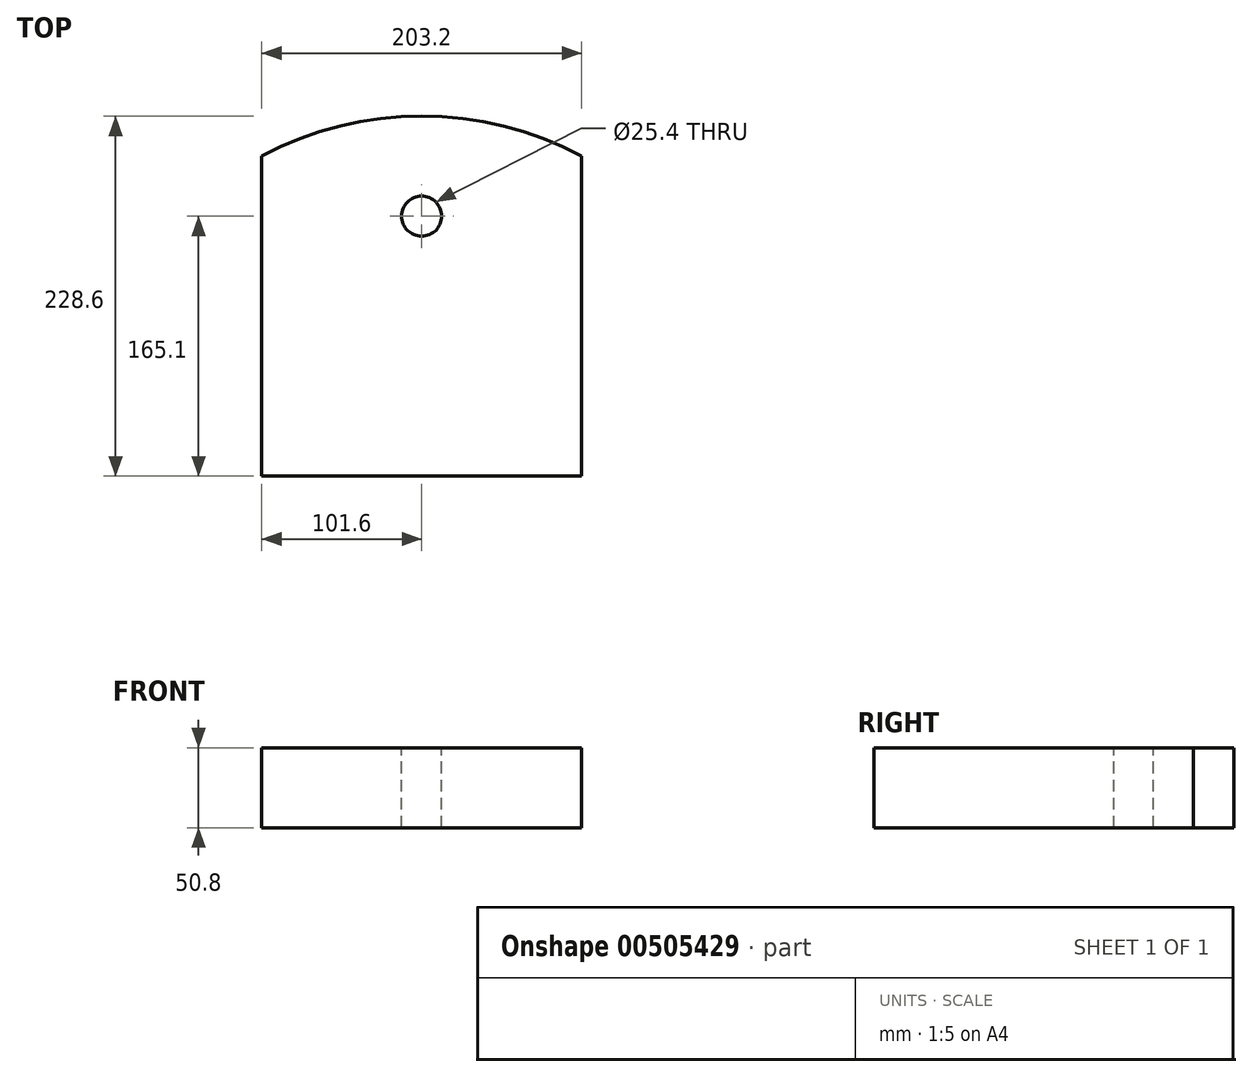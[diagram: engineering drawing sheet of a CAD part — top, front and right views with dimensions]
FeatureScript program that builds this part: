
annotation { "Feature Type Name" : "Feature", "Feature Type Description" : "" }
export const myFeature = defineFeature(function(context is Context, id is Id, definition is map)
    precondition{}
    {
        {
            var Q0;
            Q0=qCreatedBy(makeId("Top.planeOp"),FACE);
            var sketch = newSketch(context, id + "F0", { "sketchPlane" : qUnion([Q0])});
            skLineSegment(sketch, "E0", {"start": v(-101.6, 0) * mm, "end": v(-101.6, -101.6) * mm});
            skLineSegment(sketch, "E1", {"start": v(101.6, 0) * mm, "end": v(101.6, -101.6) * mm});
            skLineSegment(sketch, "E2", {"start": v(-101.6, -101.6) * mm, "end": v(101.6, -101.6) * mm});
            skLineSegment(sketch, "E3", {"start": v(-101.6, 0) * mm, "end": v(-101.6, 101.6) * mm});
            skLineSegment(sketch, "E4", {"start": v(101.6, 0) * mm, "end": v(101.6, 101.6) * mm});
            skPoint(sketch, "E5.endSnap0", {"position": v(0, -101.6) * mm});
            skArc(sketch, "E6", {"start": v(101.6, 101.6) * mm, "mid": v(0, 127) * mm, "end": v(-101.6, 101.6) * mm});
            skSolve(sketch);
        }
        {
            var Q0;
            Q0 = qSketchRegion(id + "F0", true);
            extrude(context, id + "F1", {"entities" : qUnion([Q0]), "depth" : 50.8 * mm});
        }
        {
            var Q0;
            Q0=makeQuery(id+"F1.opExtrude","CAP_FACE",FACE,{"disambiguationData":[OSD([sQuery(id+"F0.wireOp",EDGE,"E0"),sQuery(id+"F0.wireOp",EDGE,"E1"),sQuery(id+"F0.wireOp",EDGE,"E2"),sQuery(id+"F0.wireOp",EDGE,"E3"),sQuery(id+"F0.wireOp",EDGE,"E4"),sQuery(id+"F0.wireOp",EDGE,"E6")])],"isStart":false});
            var sketch = newSketch(context, id + "F2", { "sketchPlane" : qUnion([Q0])});
            skPoint(sketch, "E7.endSnap0", {"position": v(0, 127) * mm});
            skCircle(sketch, "E8", {"center": v(0, 63.5) * mm, "radius": 12.7 * mm});
            skSolve(sketch);
        }
        {
            var Q0;
            Q0 = qSketchRegion(id + "F2", true);
            extrude(context, id + "F3", {"entities" : qUnion([Q0]), "operationType" : NewBodyOperationType.REMOVE, "oppositeDirection" : true, "depth" : 50.8 * mm});
        }
    });
